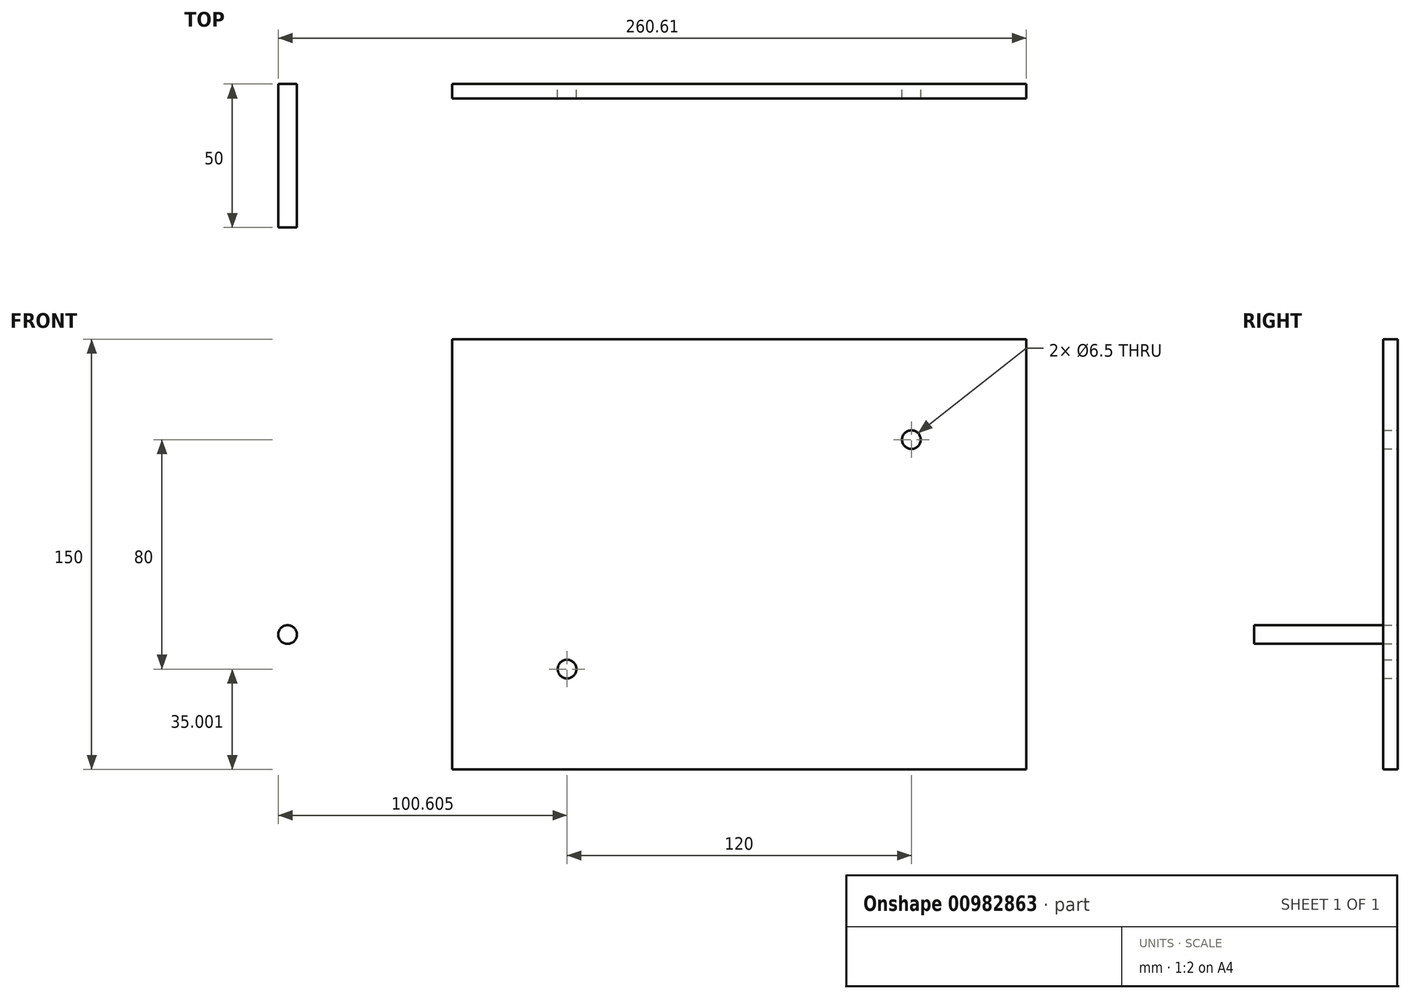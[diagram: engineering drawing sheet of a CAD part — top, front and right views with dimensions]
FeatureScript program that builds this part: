
annotation { "Feature Type Name" : "Feature", "Feature Type Description" : "" }
export const myFeature = defineFeature(function(context is Context, id is Id, definition is map)
    precondition{}
    {
        {
            var Q0;
            Q0=qCreatedBy(makeId("Front.planeOp"),FACE);
            var sketch = newSketch(context, id + "F0", { "sketchPlane" : qUnion([Q0])});
            skLineSegment(sketch, "E0.bottom", {"start": v(-94.56, 98.45) * mm, "end": v(105.44, 98.45) * mm});
            skLineSegment(sketch, "E0.top", {"start": v(-94.56, -51.55) * mm, "end": v(105.44, -51.55) * mm});
            skLineSegment(sketch, "E0.left", {"start": v(-94.56, 98.45) * mm, "end": v(-94.56, -51.55) * mm});
            skLineSegment(sketch, "E0.right", {"start": v(105.44, 98.45) * mm, "end": v(105.44, -51.55) * mm});
            skCircle(sketch, "E1", {"center": v(65.44, 63.45) * mm, "radius": 3.25 * mm});
            skCircle(sketch, "E2", {"center": v(-54.56, -16.55) * mm, "radius": 3.25 * mm});
            skCircle(sketch, "E3", {"center": v(-151.92, -4.52) * mm, "radius": 3.25 * mm});
            skSolve(sketch);
        }
        {
            var Q0;
            Q0=makeQuery(id+"F0.imprint","IMPRINT",FACE,{"disambiguationData":[TD([[makeQuery(id+"F0.imprint","IMPRINT",EDGE,{"derivedFrom":sQuery(id+"F0.wireOp",EDGE,"E0.bottom")}),-1.0]])]});
            extrude(context, id + "F1", {"entities" : qUnion([Q0]), "depth" : 5 * mm, "offsetDistance" : 25 * mm});
        }
        {
            var Q0;
            Q0=makeQuery(id+"F0.imprint","IMPRINT",FACE,{"disambiguationData":[TD([[makeQuery(id+"F0.imprint","IMPRINT",EDGE,{"derivedFrom":sQuery(id+"F0.wireOp",EDGE,"E3")}),1.0]])]});
            extrude(context, id + "F2", {"entities" : qUnion([Q0]), "depth" : 50 * mm, "offsetDistance" : 25 * mm});
        }
    });
